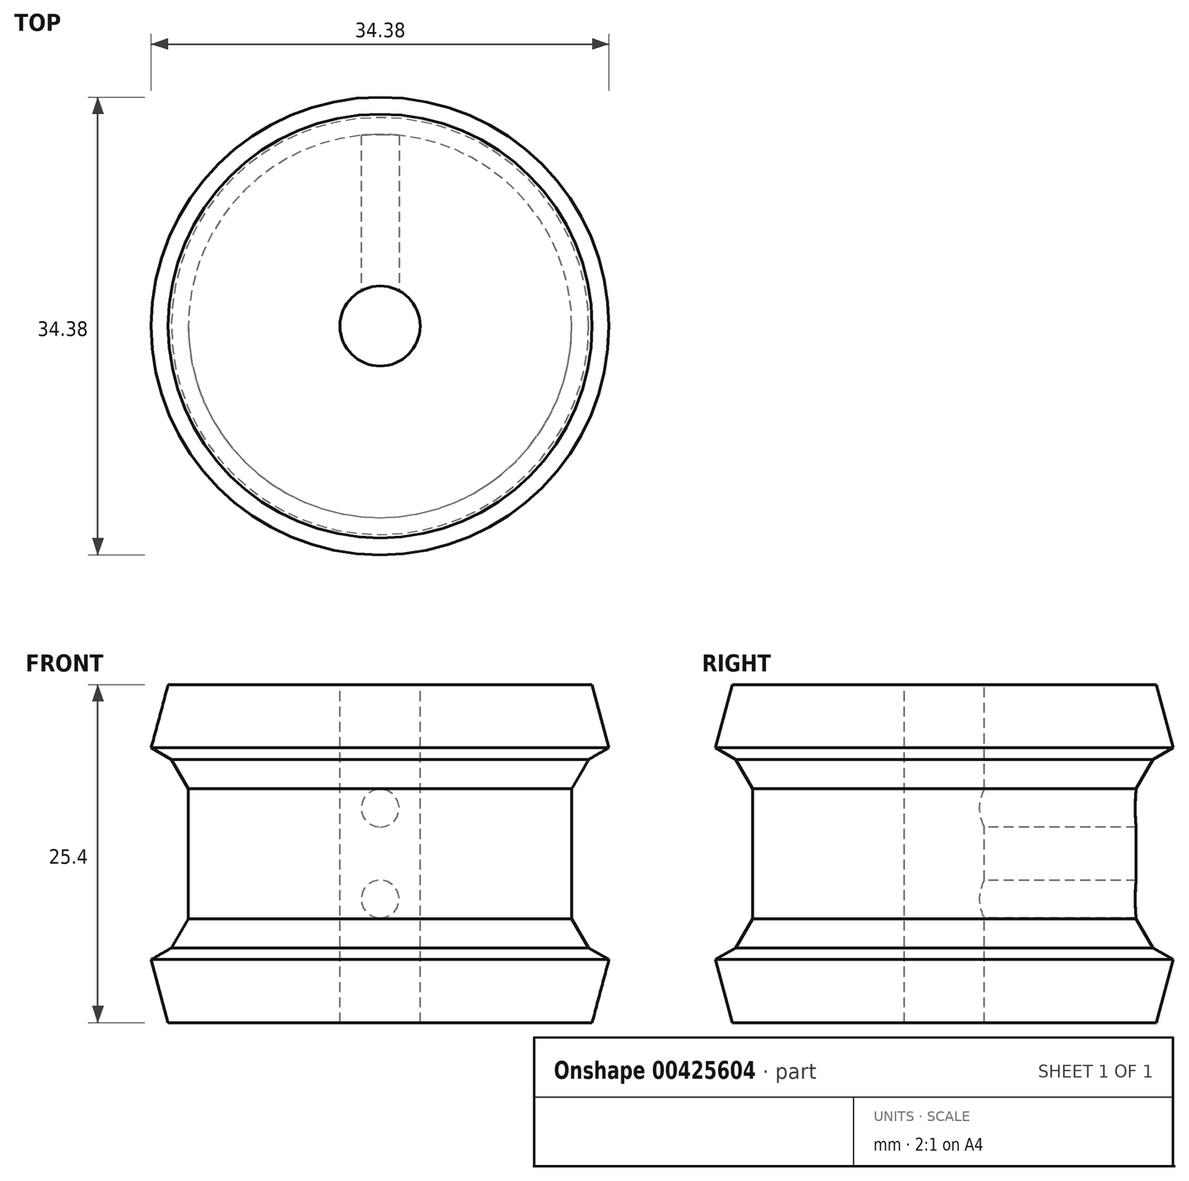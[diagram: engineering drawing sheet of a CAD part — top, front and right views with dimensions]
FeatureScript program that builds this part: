
annotation { "Feature Type Name" : "Feature", "Feature Type Description" : "" }
export const myFeature = defineFeature(function(context is Context, id is Id, definition is map)
    precondition{}
    {
        {
            var Q0;
            Q0=qCreatedBy(makeId("Front.planeOp"),FACE);
            var sketch = newSketch(context, id + "F0", { "sketchPlane" : qUnion([Q0])});
            skLineSegment(sketch, "E0", {"start": v(0, 20.36) * mm, "end": v(-25.4, 20.36) * mm});
            skLineSegment(sketch, "E1", {"start": v(-25.4, 20.36) * mm, "end": v(-14.4, 14) * mm});
            skLineSegment(sketch, "E2", {"start": v(-14.4, 14) * mm, "end": v(-14.4, 1.3) * mm});
            skLineSegment(sketch, "E3", {"start": v(-14.4, 1.3) * mm, "end": v(-25.4, -5.04) * mm});
            skLineSegment(sketch, "E4", {"start": v(-25.4, -5.04) * mm, "end": v(0, -5.04) * mm});
            skLineSegment(sketch, "E5", {"start": v(0, -5.04) * mm, "end": v(0, 20.36) * mm});
            skSolve(sketch);
        }
        {
            var Q0;
            Q0=makeQuery(id+"F0.imprint","IMPRINT",FACE,{"disambiguationData":[TD([[makeQuery(id+"F0.imprint","IMPRINT",EDGE,{"derivedFrom":sQuery(id+"F0.wireOp",EDGE,"E0")}),1.0]])]});
            var Q1;
            Q1=sQuery(id+"F0.wireOp",EDGE,"E5");
            revolve(context, id + "F1", {"entities" : qUnion([Q0]), "axis" : qUnion([Q1]), "revolveType" : RevolveType.FULL});
        }
        {
            var Q0;
            Q0=makeQuery(id+"F1.opRevolve","SWEPT_EDGE",EDGE,{"disambiguationData":[OSD([sQuery(id+"F0.wireOp",EDGE,"E0"),sQuery(id+"F0.wireOp",EDGE,"E1")])]});
            var Q1;
            Q1=makeQuery(id+"F1.opRevolve","SWEPT_EDGE",EDGE,{"disambiguationData":[OSD([sQuery(id+"F0.wireOp",EDGE,"E3"),sQuery(id+"F0.wireOp",EDGE,"E4")])]});
            var Q2;
            Q2=makeQuery(id+"F1.opRevolve","SWEPT_EDGE",EDGE,{"disambiguationData":[OSD([sQuery(id+"F0.wireOp",EDGE,"E2"),sQuery(id+"F0.wireOp",EDGE,"E3")])]});
            var Q3;
            Q3=makeQuery(id+"F1.opRevolve","SWEPT_EDGE",EDGE,{"disambiguationData":[OSD([sQuery(id+"F0.wireOp",EDGE,"E1"),sQuery(id+"F0.wireOp",EDGE,"E2")])]});
            chamfer(context, id + "F2", {"entities" : qUnion([Q0, Q1, Q2, Q3]), "width" : 2.54 * mm, "tangentPropagation" : true});
        }
        {
            var Q0;
            Q0=makeQuery(id+"F1.opRevolve","SWEPT_FACE",FACE,{"disambiguationData":[OSD([sQuery(id+"F0.wireOp",EDGE,"E0")])]});
            var sketch = newSketch(context, id + "F3", { "sketchPlane" : qUnion([Q0])});
            skCircle(sketch, "E6", {"center": v(0, 0) * mm, "radius": 3 * mm});
            skSolve(sketch);
        }
        {
            var Q0;
            Q0=makeQuery(id+"F3.imprint","IMPRINT",FACE,{"disambiguationData":[TD([[makeQuery(id+"F3.imprint","IMPRINT",EDGE,{"derivedFrom":sQuery(id+"F3.wireOp",EDGE,"E6")}),1.0]])]});
            extrude(context, id + "F4", {"entities" : qUnion([Q0]), "operationType" : NewBodyOperationType.REMOVE, "oppositeDirection" : true, "depth" : 25.4 * mm});
        }
        {
            var Q0;
            Q0=qCreatedBy(makeId("Front.planeOp"),FACE);
            var sketch = newSketch(context, id + "F5", { "sketchPlane" : qUnion([Q0])});
            skCircle(sketch, "E7", {"center": v(0, 11.07) * mm, "radius": 1.42 * mm});
            skCircle(sketch, "E8", {"center": v(0, 4.24) * mm, "radius": 1.42 * mm});
            skSolve(sketch);
        }
        {
            var Q0;
            Q0 = qSketchRegion(id + "F5", true);
            extrude(context, id + "F6", {"entities" : qUnion([Q0]), "operationType" : NewBodyOperationType.REMOVE, "oppositeDirection" : true, "depth" : 32.26 * mm});
        }
    });
